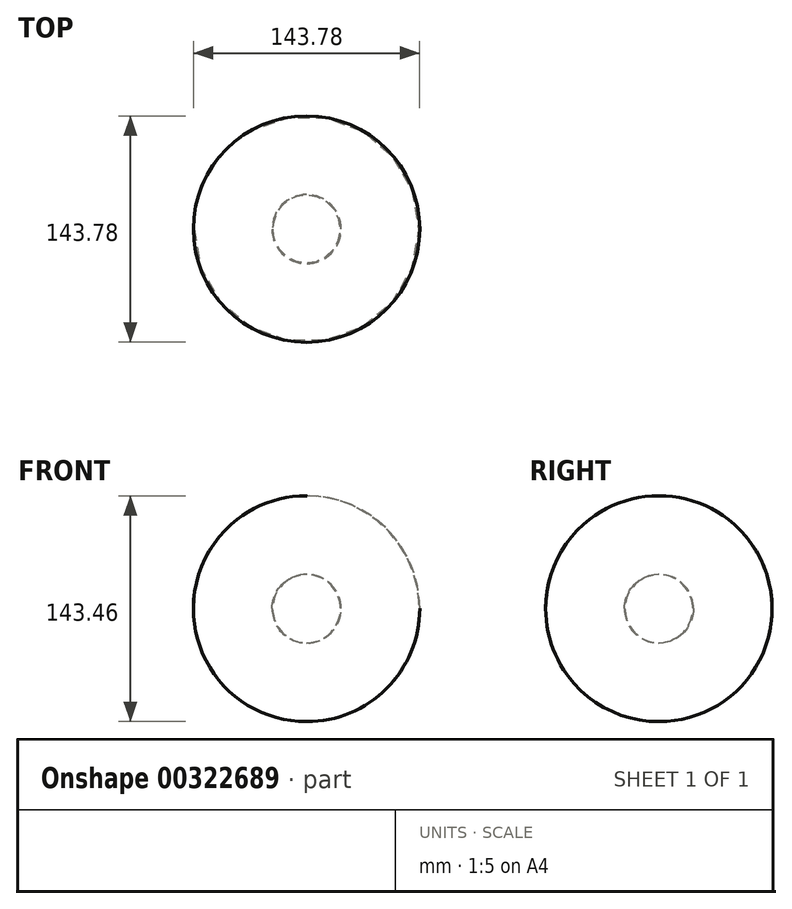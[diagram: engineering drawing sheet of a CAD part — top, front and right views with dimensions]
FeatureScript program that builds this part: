
annotation { "Feature Type Name" : "Feature", "Feature Type Description" : "" }
export const myFeature = defineFeature(function(context is Context, id is Id, definition is map)
    precondition{}
    {
        {
            var Q0;
            Q0=qCreatedBy(makeId("Right.planeOp"),FACE);
            var sketch = newSketch(context, id + "F0", { "sketchPlane" : qUnion([Q0])});
            skLineSegment(sketch, "E0", {"start": v(0, 43.46) * mm, "end": v(0, 0) * mm});
            skArc(sketch, "E1", {"start": v(0, 0) * mm, "mid": v(21.9, 21.73) * mm, "end": v(0, 43.46) * mm});
            skSolve(sketch);
        }
        {
            var Q0;
            Q0=makeQuery(id+"F0.imprint","IMPRINT",FACE,{"disambiguationData":[TD([[makeQuery(id+"F0.imprint","IMPRINT",EDGE,{"derivedFrom":sQuery(id+"F0.wireOp",EDGE,"E0")}),1.0]])]});
            var Q1;
            Q1=sQuery(id+"F0.wireOp",EDGE,"E0");
            revolve(context, id + "F1", {"entities" : qUnion([Q0]), "axis" : qUnion([Q1]), "revolveType" : RevolveType.FULL});
        }
        {
            var Q0;
            Q0=qCreatedBy(makeId("Right.planeOp"),FACE);
            var sketch = newSketch(context, id + "F2", { "sketchPlane" : qUnion([Q0])});
            skLineSegment(sketch, "E2", {"start": v(0, 21.84) * mm, "end": v(0, 14.86) * mm});
            skArc(sketch, "E3", {"start": v(0, 21.84) * mm, "mid": v(-2.75, 18.35) * mm, "end": v(0, 14.86) * mm});
            skSolve(sketch);
        }
        {
            var Q0;
            Q0=makeQuery(id+"F1.opRevolve","SWEPT_FACE",FACE,{"disambiguationData":[OSD([sQuery(id+"F0.wireOp",EDGE,"E1")])]});
            var Q1;
            Q1=makeQuery(id+"F1.opRevolve","SWEPT_BODY",BODY,{"disambiguationData":[OSD([sQuery(id+"F0.wireOp",EDGE,"E0"),sQuery(id+"F0.wireOp",EDGE,"E1")])]});
            shell(context, id + "F3", {"isHollow" : true, "entities" : qUnion([Q0]), "parts" : qUnion([Q1]), "thickness" : 50 * mm, "oppositeDirection" : true});
        }
    });
